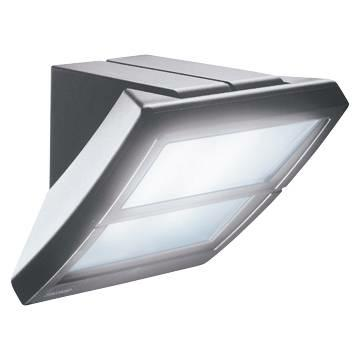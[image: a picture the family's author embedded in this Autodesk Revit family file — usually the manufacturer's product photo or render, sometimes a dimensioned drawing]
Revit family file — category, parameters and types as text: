
# Revit family: Lighting-UrbanLighting-GEWISS-EXTRO-FLOODLIGHT_MULTIFUNCTIONAL
name_source: partatom
category: Apparecchi per illuminazione
units: mm (PartAtom-declared; Revit-internal decimal feet)

## family parameters
Basato su piano di lavoro = Sì
Condiviso = No
Numero OmniClass = 23.80.70.14.21
Punto di calcolo locali = Sì
Quota connettore circolare = Usa diametro
Sempre verticale = Sì
Sorgente d'illuminazione = No
Taglio con vuoti quando caricato = No
Tipo di parte = Normale
Titolo OmniClass = Street and Roadway Lighting

## types (4) — shared parameters
Altezza da terra = 915 mm
Application = Indoor / Outdoor
Carico apparente = 0 VA
Catalogue = LIGHTING
Catalogue Range = EXTRO
Classificazione carico = Altro
Colour = Graphite grey
Cornice = GEWISS - Grigio Graffite
Electrocod = 2415
Glow Wire Test = 850°C
IDF = 7663265a-da37-4366-992a-be40d6c561e0
IDT = f88220e3-a173-4bf5-a06b-d8481c9e1565
IP degree = IP55
Immagine tipo = GW82281S.jpg
Insulation class = I
Larghezza = 260 mm  [stored 0.853018 ft]
Material = Technopolymer
Minimum distance from the illuminated object = 1M
Numero poli = 1
Operating temperature: = -25 +25 °C
Produttore = GEWISS S.p.A.
Prospetto di default = 1219 mm
SEO = Multifunction device
Shock resistance = IK09
Staffaggio = GEWISS - Grigio Graffite
Struttura = GEWISS - Grigio Graffite
Technical sheet = https://www.gewiss.com
URL = https://www.gewiss.com
Version file RFA = 20.11
Vetro led = GEWISS - Led - lm 1470 / Temp_4000 K (Ra 80)
Voltaggio = 0 V

## per-type parameters (varying)
- GW82206 - EXTRO 100W E27 G.GREY: Descrizione=EXTRO 100W E27 G.GREY; EAN code=8011564210356; Efficiency class of compatible lamps=D ÷ A+; Lamp holder=E27; Lamp included=No; Lamp power=100W; Max lamp power=100W; Modello=GW82206; System power=13W; Type of lamp=E27; Version type=Standard; Weight (kg)=2,4; Weight (kg):=2,4
- GW82246 - EXTRO GR.1X26-32W220-240V50-60HZ EM.P.1H: Accumulator type=Nickel-Cadmium; Autonomy=1H; Descrizione=EXTRO GR.1X26-32W220-240V50-60HZ EM.P.1H; Driver type=EVG electronic reactor; Duration=1H; EAN code=8011564202658; Efficiency class of compatible lamps=A; Lamp=FSM; Lamp holder=GX24q-3; Lamp power=26-32W; Luminous flux in emerg. [lm]=135 / 90; Luminous flux in emerg. [lm]:=135 / 90; Modello=GW82246; Type of lamp=FSM; Version type=Emergency; Voltage=220/240 V - 50/60 Hz; Weight (kg)=2,8; Weight (kg):=2,8
- GW82286 - EXTRO 2X26-32W 220-240V 50-60HZ G.GREY: Descrizione=EXTRO 2X26-32W 220-240V 50-60HZ G.GREY; Driver type=EVG electronic reactor; EAN code=8011564210332; Efficiency class of compatible lamps=A; Lamp=FSM; Lamp holder=GX24q-3; Lamp included=No; Lamp power=26-32W; Modello=GW82286; No. of lamps=2; No. of lamps:=2; System power=13W; Type of lamp=FSM; Version type=Standard; Voltage=220/240 V - 50/60 Hz; Weight (kg)=2,5; Weight (kg):=2,5
- GW82281S - EXTRO W/L 70W SE 230V-50HZ G.GREY: Descrizione=EXTRO W/L 70W SE 230V-50HZ G.GREY; Driver type=KCG electromagnetic reactor; EAN code=8011564210301; Efficiency class of compatible lamps=A ÷ A+; Efficiency class of the lamp supplied=A; Lamp holder=E27; Lamp included=Yes; Lamp power=70W; Lamp supplied=SE*; Modello=GW82281S; System power=13W; Type of lamp=SE; Version type=Standard; Voltage=230 V - 50 Hz; Weight (kg)=3,6; Weight (kg):=3,6

note: [stored X ft] marks values corroborated as IEEE doubles in the binary element streams (Revit-internal decimal feet)
